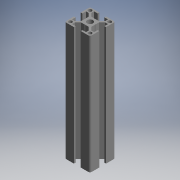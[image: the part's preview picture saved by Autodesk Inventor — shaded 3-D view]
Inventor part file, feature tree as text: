
AUTODESK INVENTOR PART (.ipt)
format: ipt  version: 2017.3 (Build 213256000, 256)  size: 209,920 bytes
history: native  units: mm (DEFAULTED — no unit token found)
features: other x21, sketch x3, hole x2, extrude x1, pattern_linear x1
ambient origin geometry x8: Origin, YZ Plane, XZ Plane, XY Plane, X Axis, Y Axis, Z Axis, Center Point
bodies: Solid1 (feature_tree)
feature tree (28):
  extrude  "Extrusion1"  Depth=140.0mm
  hole  "Hole1"  [1 undecoded]
  hole  "Hole2"  [1 undecoded]
  pattern_linear  "Rectangular Pattern1"  [2 undecoded]
  other  "C1_XY"
  other  "C1_YZ"
  other  "C1_ZX"
  other  "C1_X"
  other  "C1_Y"
  other  "C1_Z"
  other  "C1_Center"
  other  "to_frame_cap1_XY"
  other  "to_frame_cap1_YZ"
  other  "to_frame_cap1_ZX"
  other  "to_frame_cap1_X"
  other  "to_frame_cap1_Y"
  other  "to_frame_cap1_Z"
  other  "to_frame_cap1_Center"
  other  "to_frame_cap2_XY"
  other  "to_frame_cap2_YZ"
  other  "to_frame_cap2_ZX"
  other  "to_frame_cap2_X"
  other  "to_frame_cap2_Y"
  other  "to_frame_cap2_Z"
  other  "to_frame_cap2_Center"
  sketch  "Sketch_1"  dims[d0=140.0mm d1=0.0mm]
  sketch  "Sketch2"  dims[d2=6.8mm d3=6.0mm d4=4.0mm d5=2.0mm d6=90.0deg d7=140.0mm d8=0.0mm]
  sketch  "Sketch3"  dims[d9=4.2mm d10=6.0mm d11=4.0mm d12=2.0mm d13=90.0deg d14=140.0mm d15=0.0mm d16=20.0mm d18=23.2mm d19=20.0mm d21=23.2mm d22=0.0mm d23=0.0mm d24=0.0mm]
note: 4 required parameter values undecoded (feature->parameter linkage not recoverable at this tier; creation-order binding heuristic only, values carry confidence <= 0.55)
